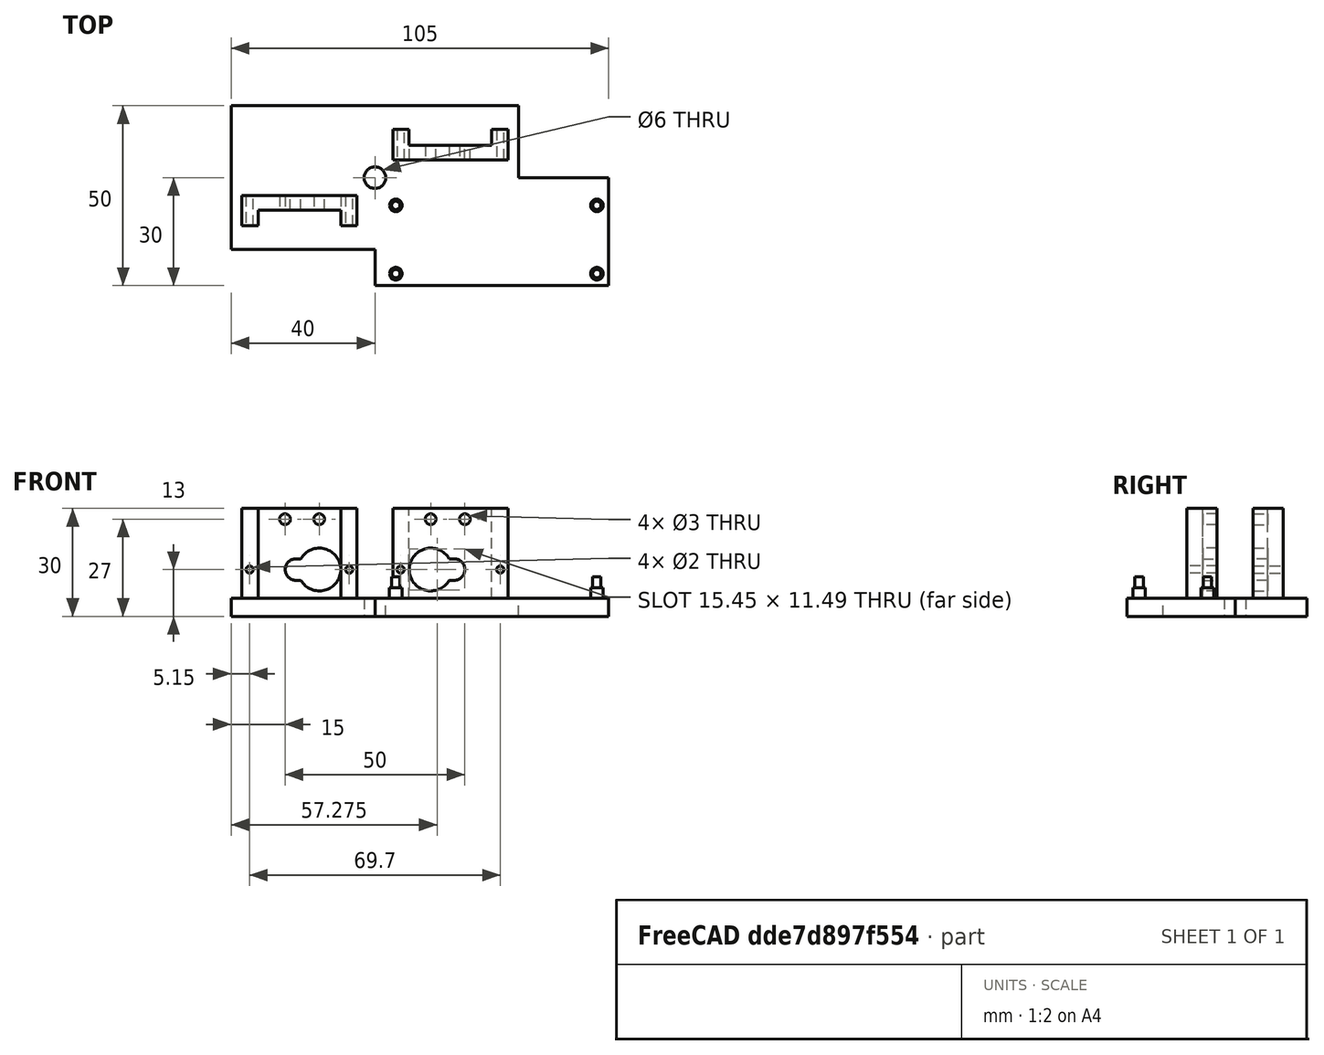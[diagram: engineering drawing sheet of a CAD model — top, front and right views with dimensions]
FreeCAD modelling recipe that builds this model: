
FCSTD DOCUMENT  (FreeCAD 1.0R39109 (Git))
Label: TrainOrderServo
License: All rights reserved
objects: Sketcher::SketchObject×6, PartDesign::Pad×4, Mesh::Feature×3, PartDesign::Pocket×2, PartDesign::CoordinateSystem×1, PartDesign::Body×1, App::Part×1
note: 32 computed .brp shape members not serialized (recipe doc carries the construction recipe); baked Part::Feature solids carry a one-line shape summary decoded from their .brp

FEATURE [Sketcher::SketchObject] Sketch
  ArcFitTolerance = 1e-06
  AttachmentSupport = -> [XY_Plane001]
  FullyConstrained = true
  MakeInternals = false
  MapMode = 5
  sketch-geometry (9):
    g0: LineSegment StartX=-40 StartY=-20 StartZ=0 EndX=0 EndY=-20 EndZ=0
    g1: LineSegment StartX=40 StartY=20 StartZ=0 EndX=-40 EndY=20 EndZ=0
    g2: LineSegment StartX=-40 StartY=20 StartZ=0 EndX=-40 EndY=-20 EndZ=0
    g3: Circle CenterX=0 CenterY=0 CenterZ=0 NormalX=0 NormalY=0 NormalZ=1 AngleXU=0 Radius=3
    g4: LineSegment StartX=0 StartY=-30 StartZ=0 EndX=65 EndY=-30 EndZ=0
    g5: LineSegment StartX=65 StartY=-30 StartZ=0 EndX=65 EndY=0 EndZ=0
    g6: LineSegment StartX=65 StartY=0 StartZ=0 EndX=40 EndY=0 EndZ=0
    g7: LineSegment StartX=0 StartY=-20 StartZ=0 EndX=0 EndY=-30 EndZ=0
    g8: LineSegment StartX=40 StartY=0 StartZ=0 EndX=40 EndY=20 EndZ=0
  constraints (24):
    c: Coincident(g8,g1)
    c: Coincident(g1,g2)
    c: Coincident(g2,g0)
    c: Horizontal(g0)
    c: Distance(g0,g1) = 40
    c: Diameter(g3) = 6
    c: Coincident(g7,g4)
    c: Coincident(g4,g5)
    c: Coincident(g5,g6)
    c: Vertical(g5)
    c: Horizontal(g4)
    c: Vertical(g8)
    c: DistanceX(g1,g1) = 80
    c: DistanceX(g-1,g6) = 40
    c: DistanceY(g7,g-1) = 20
    c: DistanceX(g-1,g5) = 65
    c: DistanceY(g4,g-1) = 30
    c: Coincident(g8,g6)
    c: Coincident(g0,g7)
    c: Tangent(g6,g-1)
    c: Tangent(g7,g-2)
    c: Horizontal(g1)
    c: Vertical(g2)
    c: Coincident(g3,g-1)
FEATURE [PartDesign::Pad] Pad
  Direction = (0,0,1)
  Length = 5
  Length2 = 10
  Profile = -> Sketch
  ReferenceAxis = -> Sketch [N_Axis]
  Suppressed = false
  Type = 0
FEATURE [Sketcher::SketchObject] Sketch001
  ArcFitTolerance = 1e-06
  AttachmentSupport = -> [Pad]
  ExternalGeometry = -> [Pad]
  FullyConstrained = true
  MakeInternals = false
  MapMode = 5
  Placement = pos=(0,0,5) rot=(0,0,1;0rad)
  sketch-geometry (16):
    g0: LineSegment StartX=5 StartY=5 StartZ=0 EndX=37 EndY=5 EndZ=0
    g1: LineSegment StartX=37 StartY=5 StartZ=0 EndX=37 EndY=13.4 EndZ=0
    g2: LineSegment StartX=37 StartY=13.4 StartZ=0 EndX=32.5 EndY=13.4 EndZ=0
    g3: LineSegment StartX=32.5 StartY=13.4 StartZ=0 EndX=32.5 EndY=9 EndZ=0
    g4: LineSegment StartX=32.5 StartY=9 StartZ=0 EndX=9.5 EndY=9 EndZ=0
    g5: LineSegment StartX=9.5 StartY=9 StartZ=0 EndX=9.5 EndY=13.4 EndZ=0
    g6: LineSegment StartX=9.5 StartY=13.4 StartZ=0 EndX=5 EndY=13.4 EndZ=0
    g7: LineSegment StartX=5 StartY=13.4 StartZ=0 EndX=5 EndY=5 EndZ=0
    g8: LineSegment StartX=-5 StartY=-5 StartZ=0 EndX=-37 EndY=-5 EndZ=0
    g9: LineSegment StartX=-37 StartY=-5 StartZ=0 EndX=-37 EndY=-13.4 EndZ=0
    g10: LineSegment StartX=-37 StartY=-13.4 StartZ=0 EndX=-32.5 EndY=-13.4 EndZ=0
    g11: LineSegment StartX=-32.5 StartY=-13.4 StartZ=0 EndX=-32.5 EndY=-9 EndZ=0
    g12: LineSegment StartX=-32.5 StartY=-9 StartZ=0 EndX=-9.5 EndY=-9 EndZ=0
    g13: LineSegment StartX=-9.5 StartY=-9 StartZ=0 EndX=-9.5 EndY=-13.4 EndZ=0
    g14: LineSegment StartX=-9.5 StartY=-13.4 StartZ=0 EndX=-5 EndY=-13.4 EndZ=0
    g15: LineSegment StartX=-5 StartY=-13.4 StartZ=0 EndX=-5 EndY=-5 EndZ=0
  constraints (48):
    c: Horizontal(g0)
    c: Coincident(g0,g1)
    c: Vertical(g1)
    c: Coincident(g1,g2)
    c: Horizontal(g2)
    c: Coincident(g2,g3)
    c: Vertical(g3)
    c: Coincident(g3,g4)
    c: Horizontal(g4)
    c: Coincident(g4,g5)
    c: Vertical(g5)
    c: Coincident(g5,g6)
    c: Horizontal(g6)
    c: Coincident(g6,g7)
    c: Coincident(g7,g0)
    c: Vertical(g7)
    c: DistanceX(g0,g0) = 32
    c: Distance(g5,g5) = 4.4
    c: Distance(g6,g6) = 4.5
    c: DistanceY(g-1,g0) = 5
    c: DistanceY(g0,g4) = 4
    c: Equal(g5,g3)
    c: Equal(g6,g2)
    c: DistanceX(g-1,g0) = 5
    c: Horizontal(g8)
    c: Coincident(g8,g9)
    c: Vertical(g9)
    c: Coincident(g9,g10)
    c: Horizontal(g10)
    c: Coincident(g10,g11)
    c: Vertical(g11)
    c: Coincident(g11,g12)
    c: Horizontal(g12)
    c: Coincident(g12,g13)
    c: Vertical(g13)
    c: Coincident(g13,g14)
    c: Horizontal(g14)
    c: Coincident(g14,g15)
    c: Coincident(g15,g8)
    c: Vertical(g15)
    c: DistanceY(g8,g-1) = 5
    c: DistanceX(g8,g-1) = 5
    c: Equal(g8,g0)
    c: Equal(g15,g9)
    c: Equal(g10,g14)
    c: Equal(g15,g7)
    c: Equal(g14,g6)
    c: Equal(g13,g5)
FEATURE [PartDesign::Pad] Pad001
  BaseFeature = -> Pad
  Direction = (0,0,1)
  Length = 25
  Length2 = 10
  Profile = -> Sketch001
  ReferenceAxis = -> Sketch001 [N_Axis]
  Suppressed = false
  Type = 0
FEATURE [Sketcher::SketchObject] Sketch002
  ArcFitTolerance = 1e-06
  AttachmentSupport = -> [Pad001]
  ExternalGeometry = -> [Pad001]
  FullyConstrained = true
  MakeInternals = false
  MapMode = 5
  Placement = pos=(0,-9,0) rot=(1,0,0;1.5708rad)
  sketch-geometry (8):
    g0: ArcOfCircle CenterX=-15.45 CenterY=13 CenterZ=0 NormalX=0 NormalY=0 NormalZ=1 AngleXU=0 Radius=5.95 StartAngle=3.67005 EndAngle=8.89632
    g1: Circle CenterX=-7.15 CenterY=13 CenterZ=0 NormalX=0 NormalY=0 NormalZ=1 AngleXU=0 Radius=1
    g2: Circle CenterX=-34.85 CenterY=13 CenterZ=0 NormalX=0 NormalY=0 NormalZ=1 AngleXU=0 Radius=1
    g3: ArcOfCircle CenterX=-21.95 CenterY=13 CenterZ=0 NormalX=0 NormalY=0 NormalZ=1 AngleXU=0 Radius=3 StartAngle=1.5708 EndAngle=4.71239
    g4: LineSegment StartX=-21.95 StartY=10 StartZ=0 EndX=-20.5883 EndY=10 EndZ=0
    g5: LineSegment StartX=-21.95 StartY=16 StartZ=0 EndX=-20.5883 EndY=16 EndZ=0
    g6: Circle CenterX=-25 CenterY=27 CenterZ=0 NormalX=0 NormalY=0 NormalZ=1 AngleXU=0 Radius=1.5
    g7: Circle CenterX=-15.5 CenterY=27 CenterZ=0 NormalX=0 NormalY=0 NormalZ=1 AngleXU=0 Radius=1.5
  constraints (24):
    c: Diameter(g0) = 11.9
    c: DistanceY(g-4,g0) = 8
    c: Tangent(g0,g-4)
    c: Diameter(g1) = 2
    c: Diameter(g2) = 2
    c: Horizontal(g1,g0)
    c: Horizontal(g0,g2)
    c: DistanceX(g2,g-5) = 2.35
    c: DistanceX(g-5,g1) = 2.35
    c: Diameter(g3) = 6
    c: Horizontal(g3,g0)
    c: DistanceX(g3,g0) = 6.5
    c: Horizontal(g4)
    c: Horizontal(g5)
    c: Diameter(g6) = 3
    c: Diameter(g7) = 3
    c: Horizontal(g6,g7)
    c: DistanceX(g6,g7) = 9.5
    c: DistanceX(g7,g-4) = 6
    c: Tangent(g3,g5) = 1.5708
    c: Tangent(g3,g4) = -1.5708
    c: Coincident(g0,g4)
    c: Coincident(g0,g5)
    c: DistanceY(g0,g7) = 14
FEATURE [PartDesign::Pocket] Pocket
  BaseFeature = -> Pad001
  Direction = (0,1,-2e-16)
  Length = 5
  Length2 = 5
  Midplane = true
  Profile = -> Sketch002
  ReferenceAxis = -> Sketch002 [N_Axis]
  Suppressed = false
  Type = 1
FEATURE [PartDesign::CoordinateSystem] Local_CS
  AttacherType = Attacher::AttachEngine3D
  AttachmentSupport = -> [Pocket]
  MapMode = 5
  Placement = pos=(0,9,0) rot=(0,0.707107,0.707107;3.14159rad)
FEATURE [Sketcher::SketchObject] Sketch003
  ArcFitTolerance = 1e-06
  AttachmentSupport = -> [Pocket]
  ExternalGeometry = -> [Pocket]
  FullyConstrained = true
  MakeInternals = false
  MapMode = 5
  Placement = pos=(0,9,0) rot=(0,0.707107,0.707107;3.14159rad)
  sketch-geometry (8):
    g0: ArcOfCircle CenterX=-22 CenterY=13 CenterZ=0 NormalX=0 NormalY=0 NormalZ=1 AngleXU=0 Radius=3 StartAngle=1.5708 EndAngle=4.71239
    g1: Circle CenterX=-25 CenterY=27 CenterZ=0 NormalX=0 NormalY=0 NormalZ=1 AngleXU=0 Radius=1.5
    g2: Circle CenterX=-15.5 CenterY=27 CenterZ=0 NormalX=0 NormalY=0 NormalZ=1 AngleXU=0 Radius=1.5
    g3: Circle CenterX=-7.15 CenterY=13 CenterZ=0 NormalX=0 NormalY=0 NormalZ=1 AngleXU=0 Radius=1
    g4: Circle CenterX=-34.85 CenterY=13 CenterZ=0 NormalX=0 NormalY=0 NormalZ=1 AngleXU=0 Radius=1
    g5: LineSegment StartX=-22 StartY=16 StartZ=0 EndX=-20.6383 EndY=16 EndZ=0
    g6: LineSegment StartX=-22 StartY=10 StartZ=0 EndX=-20.6383 EndY=10 EndZ=0
    g7: ArcOfCircle CenterX=-15.5 CenterY=13 CenterZ=0 NormalX=0 NormalY=0 NormalZ=1 AngleXU=0 Radius=5.95 StartAngle=3.67005 EndAngle=8.89632
  constraints (25):
    c: Diameter(g0) = 6
    c: Diameter(g1) = 3
    c: Diameter(g2) = 3
    c: Diameter(g3) = 2
    c: Diameter(g4) = 2
    c: Horizontal(g1,g2)
    c: Horizontal(g3,g4)
    c: DistanceX(g1,g2) = 9.5
    c: Horizontal(g5)
    c: Horizontal(g6)
    c: Diameter(g7) = 11.9
    c: DistanceX(g0,g7) = 6.5
    c: Horizontal(g4,g0)
    c: Horizontal(g0,g7)
    c: Vertical(g7,g2)
    c: DistanceY(g7,g2) = 14
    c: Tangent(g0,g5) = 1.5708
    c: Coincident(g7,g5)
    c: Coincident(g7,g6)
    c: DistanceY(g-4,g7) = 8
    c: DistanceX(g7,g-3) = 6
    c: DistanceX(g-3,g3) = 2.35
    c: DistanceX(g4,g-5) = 2.35
    c: Equal(g6,g5)
    c: Coincident(g6,g0)
FEATURE [PartDesign::Pocket] Pocket001
  BaseFeature = -> Pocket
  Direction = (0,-1,2e-16)
  Length = 5
  Length2 = 5
  Midplane = true
  Profile = -> Sketch003
  ReferenceAxis = -> Sketch003 [N_Axis]
  Suppressed = false
  Type = 1
FEATURE [Mesh::Feature] Mesh  label="Pocket001 (Meshed)"
FEATURE [Sketcher::SketchObject] Sketch004
  ArcFitTolerance = 1e-06
  AttachmentSupport = -> [Pocket001]
  ExternalGeometry = -> [Pocket001]
  FullyConstrained = true
  MakeInternals = false
  MapMode = 5
  Placement = pos=(0,0,5) rot=(0,0,1;0rad)
  sketch-geometry (4):
    g0: Circle CenterX=61.7 CenterY=-26.7 CenterZ=0 NormalX=0 NormalY=0 NormalZ=1 AngleXU=0 Radius=1.75
    g1: Circle CenterX=61.7 CenterY=-7.7 CenterZ=0 NormalX=0 NormalY=0 NormalZ=1 AngleXU=0 Radius=1.75
    g2: Circle CenterX=5.8 CenterY=-7.7 CenterZ=0 NormalX=0 NormalY=0 NormalZ=1 AngleXU=0 Radius=1.75
    g3: Circle CenterX=5.8 CenterY=-26.7 CenterZ=0 NormalX=0 NormalY=0 NormalZ=1 AngleXU=0 Radius=1.75
  constraints (12):
    c: Diameter(g0) = 3.5
    c: Diameter(g1) = 3.5
    c: Diameter(g2) = 3.5
    c: Diameter(g3) = 3.5
    c: DistanceY(g-4,g0) = 3.3
    c: DistanceX(g0,g-4) = 3.3
    c: Horizontal(g3,g0)
    c: Horizontal(g2,g1)
    c: Vertical(g2,g3)
    c: Vertical(g1,g0)
    c: DistanceY(g0,g1) = 19
    c: DistanceX(g3,g0) = 55.9
FEATURE [PartDesign::Pad] Pad002
  BaseFeature = -> Pocket001
  Direction = (0,0,1)
  Length = 3
  Length2 = 10
  Profile = -> Sketch004
  ReferenceAxis = -> Sketch004 [N_Axis]
  Suppressed = false
  Type = 0
FEATURE [Mesh::Feature] Mesh001  label="Pad002 (Meshed)"
FEATURE [Sketcher::SketchObject] Sketch005
  ArcFitTolerance = 1e-06
  AttachmentSupport = -> [Pad002]
  ExternalGeometry = -> [Pad002]
  FullyConstrained = true
  MakeInternals = false
  MapMode = 5
  Placement = pos=(0,0,8) rot=(0,0,1;0rad)
  sketch-geometry (4):
    g0: Circle CenterX=5.8 CenterY=-7.7 CenterZ=0 NormalX=0 NormalY=0 NormalZ=1 AngleXU=0 Radius=1.15
    g1: Circle CenterX=5.8 CenterY=-26.7 CenterZ=0 NormalX=0 NormalY=0 NormalZ=1 AngleXU=0 Radius=1.15
    g2: Circle CenterX=61.7 CenterY=-26.7 CenterZ=0 NormalX=0 NormalY=0 NormalZ=1 AngleXU=0 Radius=1.15
    g3: Circle CenterX=61.7 CenterY=-7.7 CenterZ=0 NormalX=0 NormalY=0 NormalZ=1 AngleXU=0 Radius=1.15
  constraints (8):
    c: Diameter(g0) = 2.3
    c: Coincident(g0,g-3)
    c: Diameter(g1) = 2.3
    c: Coincident(g1,g-4)
    c: Diameter(g2) = 2.3
    c: Coincident(g2,g-5)
    c: Diameter(g3) = 2.3
    c: Coincident(g3,g-6)
FEATURE [PartDesign::Pad] Pad003
  BaseFeature = -> Pad002
  Direction = (0,0,1)
  Length = 3
  Length2 = 10
  Profile = -> Sketch005
  ReferenceAxis = -> Sketch005 [N_Axis]
  Suppressed = false
  Type = 0
FEATURE [PartDesign::Body] Body
  AllowCompound = false
  Group = -> [Sketch,Pad,Sketch001,Pad001,Sketch002,Pocket,Local_CS,Sketch003,Pocket001,Sketch004,Pad002,Sketch005,Pad003]
  Origin = -> Origin001
  Tip = -> Pad003
FEATURE [App::Part] Part  label="ServoBase"
  Group = -> [Body]
  Origin = -> Origin
FEATURE [Mesh::Feature] Mesh002  label="Pad003 (Meshed)"
